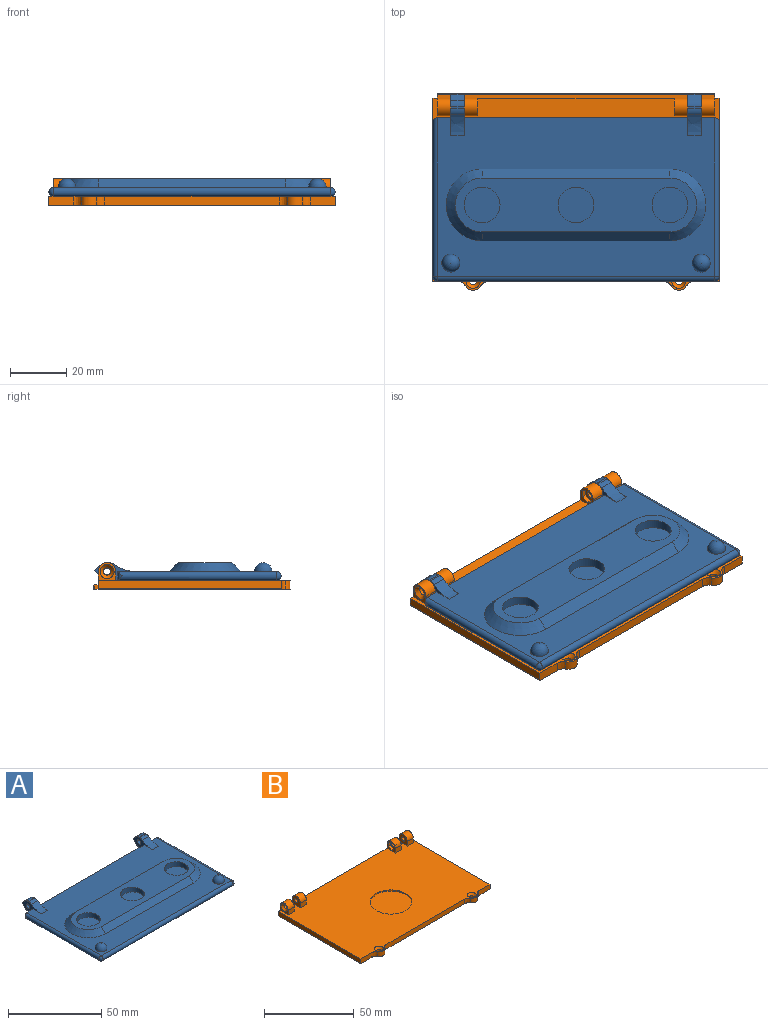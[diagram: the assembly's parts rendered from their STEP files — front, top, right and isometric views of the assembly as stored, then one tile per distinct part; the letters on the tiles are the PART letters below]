
ASSEMBLY  parts=2 mates=1
PART A: 45 faces, bbox 102.7x67.3x7.5 mm
  f0: cylinder r=3.17mm len=4.78mm, axis (-1,0,0), area 13.2mm2, adj f6,f20,f21,f33
  f1: cylinder r=3.17mm len=4.78mm, axis (-1,0,0), area 11.4mm2, adj f23,f24,f25,f30
  f2: plane 4.76x3.18mm, normal (0,1,0), area 15.1mm2, adj f4,f6,f24,f41
  f3: plane 79.35x3.18mm, normal (0,1,0), area 251.9mm2, adj f4,f6,f21,f23
  f4: plane 98.43x56.36mm, normal (0,0,1), area 3222.5mm2, adj f2,f3,f5,f14,f15,f16,f17,f18
  f5: plane 4.76x3.18mm, normal (0,1,0), area 15.1mm2, adj f4,f6,f20,f38
  f6: plane 98.43x60.18mm, normal (0,0,-1), area 5583.3mm2, adj f0,f2,f3,f5,f20,f21,f23,f24
  f7: cylinder r=6.35mm len=12.7mm, axis (0,0,-1), area 126.7mm2, adj f10,f11
  f8: cylinder r=6.35mm len=12.7mm, axis (0,0,-1), area 126.7mm2, adj f10,f12
  f9: cylinder r=6.35mm len=12.7mm, axis (0,0,-1), area 126.7mm2, adj f10,f13
  f10: plane 85.73x19.05mm, normal (0,0,1), area 1175.2mm2, adj f7,f8,f9,f14,f15,f16,f17
  f11: plane 12.7x12.7mm, normal (0,0,1), area 126.7mm2, adj f7
  f12: plane 12.7x12.7mm, normal (0,0,1), area 126.7mm2, adj f8
  f13: plane 12.7x12.7mm, normal (0,0,1), area 126.7mm2, adj f9
  f14: plane 66.68x3.18mm, normal (0,-0.71,0.71), area 299.4mm2, adj f4,f10,f15,f16
  f15: cone r=9.53mm half-angle=45deg, axis (0,0,-1), area 156.8mm2, adj f4,f10,f14,f17
  f16: cone r=9.53mm half-angle=45deg, axis (0,0,-1), area 156.8mm2, adj f4,f10,f14,f17
  f17: plane 66.68x3.18mm, normal (0,0.71,0.71), area 299.4mm2, adj f4,f10,f15,f16
  f18: sphere r=3.17mm, area 63.3mm2, adj f4
  f19: sphere r=3.17mm, area 63.3mm2, adj f4
  f20: plane 15.72x7.45mm, normal (1,0,0), area 38.8mm2, adj f0,f4,f5,f6,f22,f28,f29,f32
  f21: plane 15.72x7.45mm, normal (-1,0,0), area 38.8mm2, adj f0,f3,f4,f6,f22,f28,f29,f32
  f22: plane 4.78x0.65mm, normal (0,0,1), area 3.1mm2, adj f20,f21,f28,f29
  f23: plane 15.75x7.45mm, normal (1,0,0), area 38.9mm2, adj f1,f3,f4,f6,f25,f26,f27,f30
  f24: plane 15.75x7.45mm, normal (-1,0,0), area 38.9mm2, adj f1,f2,f4,f6,f25,f26,f27,f30
  f25: plane 4.78x0.65mm, normal (0,0,1), area 3.1mm2, adj f1,f23,f24,f27
  f26: cylinder r=3.17mm len=4.78mm, axis (-1,0,0), area 13.2mm2, adj f6,f23,f24,f31
  f27: cylinder r=3.17mm len=4.78mm, axis (1,0,0), area 9.8mm2, adj f23,f24,f25,f34
  f28: cylinder r=3.17mm len=4.78mm, axis (-1,0,0), area 13.1mm2, adj f20,f21,f22,f32
  f29: cylinder r=3.17mm len=4.78mm, axis (1,0,0), area 9.8mm2, adj f20,f21,f22,f35
  f30: plane 4.78x2.3mm, normal (0,0.64,0.77), area 14.3mm2, adj f1,f23,f24,f31
  f31: plane 4.78x2.43mm, normal (0,0.77,-0.64), area 15.1mm2, adj f23,f24,f26,f30
  f32: plane 4.78x2.03mm, normal (0,0.64,0.77), area 12.7mm2, adj f20,f21,f28,f33
  f33: plane 4.78x2.4mm, normal (0,0.77,-0.64), area 15mm2, adj f0,f20,f21,f32
  f34: bspline ~7.62x5.25mm, area 39.1mm2, adj f4,f23,f24,f27
  f35: bspline ~7.62x5.25mm, area 39.1mm2, adj f4,f20,f21,f29
  f36: cylinder r=1.27mm len=4.78mm, axis (-1,0,0), area 38.1mm2, adj f23,f24
  f37: cylinder r=1.27mm len=4.78mm, axis (1,0,0), area 38.1mm2, adj f20,f21
  f38: cylinder r=1.59mm len=3.18mm, axis (0,0,1), area 4mm2, adj f5,f39
  f39: cylinder r=1.59mm len=56.36mm, axis (0,-1,0), area 277.1mm2, adj f4,f6,f38,f40
  f40: sphere r=1.59mm, area 7.9mm2, adj f39,f42
  f41: cylinder r=1.59mm len=3.18mm, axis (0,0,-1), area 4mm2, adj f2,f43
  f42: cylinder r=1.59mm len=98.43mm, axis (-1,0,0), area 490.9mm2, adj f4,f6,f40,f44
  f43: cylinder r=1.59mm len=56.36mm, axis (0,1,0), area 277.1mm2, adj f4,f6,f41,f44
  f44: sphere r=1.59mm, area 7.9mm2, adj f42,f43
PART B: 66 faces, bbox 102x70.2x10.1 mm
  f0: plane 6.35x6.35mm, normal (-1,0,0), area 16.2mm2, adj f2,f11,f39,f41,f51,f52,f53,f54
  f1: plane 6.35x6.35mm, normal (1,0,0), area 16.2mm2, adj f2,f11,f34,f42,f44,f45,f46,f47
  f2: plane 101.97x68.62mm, normal (0,0,1), area 6061.6mm2, adj f0,f1,f3,f4,f5,f9,f10,f11
  f3: plane 8.8x3.18mm, normal (0,-1,0), area 27.9mm2, adj f2,f5,f8,f17,f29
  f4: plane 62x3.18mm, normal (0,-1,0), area 196.9mm2, adj f2,f8,f16,f18
  f5: plane 65.08x2.92mm, normal (1,0,0), area 190.1mm2, adj f2,f3,f11,f29
  f6: plane 97.94x1.09mm, normal (0,1,0), area 107mm2, adj f24,f25,f26,f27
  f7: plane 98.45x1.32mm, normal (0,0,1), area 130mm2, adj f11,f12,f13,f26
  f8: plane 101.46x69.94mm, normal (0,0,-1), area 6733.1mm2, adj f3,f4,f9,f11,f12,f13,f14,f15
  f9: plane 8.8x3.18mm, normal (0,-1,0), area 27.9mm2, adj f2,f8,f10,f19,f28
  f10: plane 65.08x2.92mm, normal (-1,0,0), area 190.1mm2, adj f2,f9,f11,f28
  f11: plane 101.6x6.35mm, normal (0,1,0), area 225.5mm2, adj f0,f1,f2,f5,f7,f8,f10,f12
  f12: plane 1.6x1.32mm, normal (1,0,0), area 2.1mm2, adj f7,f8,f11,f27
  f13: plane 1.6x1.32mm, normal (-1,0,0), area 2.1mm2, adj f7,f8,f11,f24
  f14: cylinder r=3.17mm len=5.5mm, axis (0,0,1), area 21.1mm2, adj f2,f8,f16,f17
  f15: cylinder r=3.17mm len=5.5mm, axis (0,0,-1), area 21.1mm2, adj f2,f8,f18,f19
  f16: bspline ~3.49x2.75mm, area 10.6mm2, adj f2,f4,f8,f14
  f17: bspline ~3.49x2.75mm, area 10.6mm2, adj f2,f3,f8,f14
  f18: bspline ~3.49x2.75mm, area 10.6mm2, adj f2,f4,f8,f15
  f19: bspline ~3.49x2.75mm, area 10.6mm2, adj f2,f8,f9,f15
  f20: cylinder r=1.27mm len=2.54mm, axis (0,0,1), area 14.2mm2, adj f8,f22
  f21: cylinder r=1.27mm len=2.54mm, axis (0,0,1), area 14.2mm2, adj f8,f23
  f22: cone r=1.27mm half-angle=41deg, axis (0,0,1), area 21.8mm2, adj f2,f20
  f23: cone r=1.27mm half-angle=41deg, axis (0,0,1), area 21.8mm2, adj f2,f21
  f24: cylinder r=0.25mm len=1.6mm, axis (0,0,-1), area 0.5mm2, adj f6,f13,f25,f26
  f25: cylinder r=0.25mm len=98.45mm, axis (1,0,0), area 39.2mm2, adj f6,f8,f24,f27
  f26: cylinder r=0.25mm len=98.45mm, axis (-1,0,0), area 39.2mm2, adj f6,f7,f24,f27
  f27: cylinder r=0.25mm len=1.6mm, axis (0,0,1), area 0.5mm2, adj f6,f12,f25,f26
  f28: cylinder r=0.25mm len=65.08mm, axis (0,1,0), area 26mm2, adj f8,f9,f10,f11
  f29: cylinder r=0.25mm len=65.08mm, axis (0,-1,0), area 26mm2, adj f3,f5,f8,f11
  f30: plane 6.35x6.35mm, normal (-1,0,0), area 16.6mm2, adj f2,f11,f31,f43,f63
  f31: plane 4.76x3.18mm, normal (0,-1,0), area 15.1mm2, adj f2,f30,f32,f43
  f32: plane 6.35x6.35mm, normal (1,0,0), area 30.9mm2, adj f2,f11,f31,f43,f61
  f33: plane 6.35x6.35mm, normal (-1,0,0), area 30.9mm2, adj f2,f11,f34,f42,f59
  f34: plane 4.76x3.18mm, normal (0,-1,0), area 15.1mm2, adj f1,f2,f33,f42
  f35: plane 6.35x6.35mm, normal (1,0,0), area 16.6mm2, adj f2,f11,f37,f40,f62
  f36: plane 6.35x6.35mm, normal (-1,0,0), area 30.9mm2, adj f2,f11,f37,f40,f60
  f37: plane 4.76x3.18mm, normal (0,-1,0), area 15.1mm2, adj f2,f35,f36,f40
  f38: plane 6.35x6.35mm, normal (1,0,0), area 30.9mm2, adj f2,f11,f39,f41,f58
  f39: plane 4.76x3.18mm, normal (0,-1,0), area 15.1mm2, adj f0,f2,f38,f41
  f40: cylinder r=3.17mm len=6.35mm, axis (-1,0,0), area 47.5mm2, adj f11,f35,f36,f37
  f41: cylinder r=3.17mm len=6.35mm, axis (-1,0,0), area 47.5mm2, adj f0,f11,f38,f39
  f42: cylinder r=3.17mm len=6.35mm, axis (-1,0,0), area 47.5mm2, adj f1,f11,f33,f34
  f43: cylinder r=3.17mm len=6.35mm, axis (-1,0,0), area 47.5mm2, adj f11,f30,f31,f32
  f44: plane 2.39x1.6mm, normal (0,0.5,-0.87), area 4.4mm2, adj f1,f45,f49,f50
  f45: plane 2.76x1.6mm, normal (0,1,0), area 4.4mm2, adj f1,f44,f46,f50
  f46: plane 2.39x1.6mm, normal (0,0.5,0.87), area 4.4mm2, adj f1,f45,f47,f50
  f47: plane 2.39x1.6mm, normal (0,-0.5,0.87), area 4.4mm2, adj f1,f46,f48,f50
  f48: plane 2.76x1.6mm, normal (0,-1,0), area 4.4mm2, adj f1,f47,f49,f50
  f49: plane 2.39x1.6mm, normal (0,-0.5,-0.87), area 4.4mm2, adj f1,f44,f48,f50
  f50: plane 5.51x4.78mm, normal (1,0,0), area 14.7mm2, adj f44,f45,f46,f47,f48,f49,f59
  f51: plane 2.39x1.59mm, normal (0,-0.5,-0.87), area 4.4mm2, adj f0,f52,f56,f57
  f52: plane 2.76x1.59mm, normal (0,-1,0), area 4.4mm2, adj f0,f51,f53,f57
  f53: plane 2.39x1.59mm, normal (0,-0.5,0.87), area 4.4mm2, adj f0,f52,f54,f57
  f54: plane 2.39x1.59mm, normal (0,0.5,0.87), area 4.4mm2, adj f0,f53,f55,f57
  f55: plane 2.76x1.59mm, normal (0,1,0), area 4.4mm2, adj f0,f54,f56,f57
  f56: plane 2.39x1.59mm, normal (0,0.5,-0.87), area 4.4mm2, adj f0,f51,f55,f57
  f57: plane 5.51x4.78mm, normal (-1,0,0), area 14.7mm2, adj f51,f52,f53,f54,f55,f56,f58
  f58: cylinder r=1.27mm len=3.18mm, axis (-1,0,0), area 25.3mm2, adj f38,f57
  f59: cylinder r=1.27mm len=3.16mm, axis (1,0,0), area 25.2mm2, adj f33,f50
  f60: cylinder r=1.27mm len=3.37mm, axis (1,0,0), area 26.9mm2, adj f36,f62
  f61: cylinder r=1.27mm len=3.37mm, axis (-1,0,0), area 26.9mm2, adj f32,f63
  f62: cone r=1.27mm half-angle=41deg, axis (1,0,0), area 21.8mm2, adj f35,f60
  f63: cone r=1.27mm half-angle=41deg, axis (-1,0,0), area 21.8mm2, adj f30,f61
  f64: cylinder r=11.63mm len=23.26mm, axis (0,0,1), area 57.9mm2, adj f2,f65
  f65: plane 23.26x23.26mm, normal (0,0,1), area 425mm2, adj f64
PLACE A rot(axis=(-1,0,0),0deg) t=(0.61,0,-1.71)mm
PLACE B t=(0.61,1.92,-4.89)mm fixed
MATE revolute A.f0 <-> B.f43  axis (-1,0,0) through (-43.84,30.42,1.46)mm
